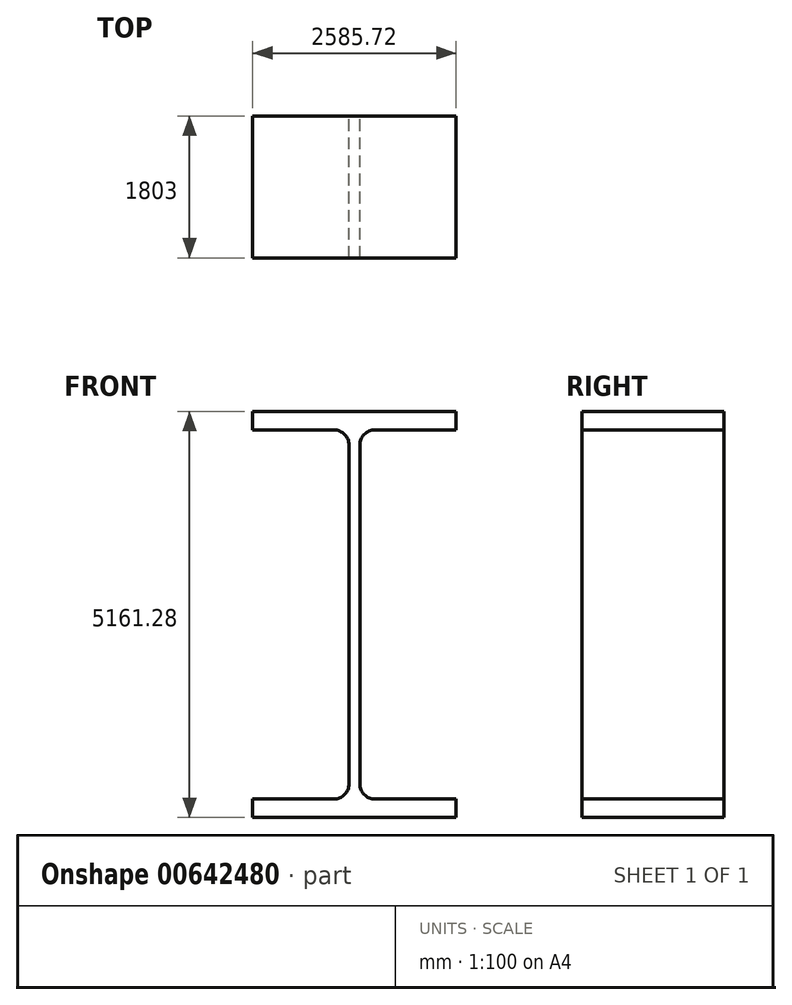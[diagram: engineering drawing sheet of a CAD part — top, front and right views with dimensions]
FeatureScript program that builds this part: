
annotation { "Feature Type Name" : "Feature", "Feature Type Description" : "" }
export const myFeature = defineFeature(function(context is Context, id is Id, definition is map)
    precondition{}
    {
        {
            var Q0;
            Q0=qCreatedBy(makeId("Front.planeOp"),FACE);
            var sketch = newSketch(context, id + "F0", { "sketchPlane" : qUnion([Q0])});
            skLineSegment(sketch, "E0", {"start": v(-1292.86, 2580.64) * mm, "end": v(-1292.86, 2344.42) * mm});
            skLineSegment(sketch, "E1", {"start": v(-1292.86, 2344.42) * mm, "end": v(-261.62, 2344.42) * mm});
            skArc(sketch, "E2", {"start": v(-261.62, 2344.42) * mm, "mid": v(-125.12, 2287.88) * mm, "end": v(-68.58, 2151.38) * mm});
            skLineSegment(sketch, "E3", {"start": v(-68.58, 2151.38) * mm, "end": v(-68.58, -2151.38) * mm});
            skArc(sketch, "E4", {"start": v(-68.58, -2151.38) * mm, "mid": v(-125.12, -2287.88) * mm, "end": v(-261.62, -2344.42) * mm});
            skLineSegment(sketch, "E5", {"start": v(-261.62, -2344.42) * mm, "end": v(-1292.86, -2344.42) * mm});
            skLineSegment(sketch, "E6", {"start": v(-1292.86, -2344.42) * mm, "end": v(-1292.86, -2580.64) * mm});
            skLineSegment(sketch, "E7", {"start": v(-1292.86, -2580.64) * mm, "end": v(1292.86, -2580.64) * mm});
            skLineSegment(sketch, "E8", {"start": v(1292.86, -2580.64) * mm, "end": v(1292.86, -2344.42) * mm});
            skLineSegment(sketch, "E9", {"start": v(1292.86, -2344.42) * mm, "end": v(261.62, -2344.42) * mm});
            skArc(sketch, "E10", {"start": v(261.62, -2344.42) * mm, "mid": v(125.12, -2287.88) * mm, "end": v(68.58, -2151.38) * mm});
            skLineSegment(sketch, "E11", {"start": v(68.58, -2151.38) * mm, "end": v(68.58, 2151.38) * mm});
            skArc(sketch, "E12", {"start": v(68.58, 2151.38) * mm, "mid": v(125.12, 2287.88) * mm, "end": v(261.62, 2344.42) * mm});
            skLineSegment(sketch, "E13", {"start": v(261.62, 2344.42) * mm, "end": v(1292.86, 2344.42) * mm});
            skLineSegment(sketch, "E14", {"start": v(1292.86, 2344.42) * mm, "end": v(1292.86, 2580.64) * mm});
            skLineSegment(sketch, "E15", {"start": v(1292.86, 2580.64) * mm, "end": v(-1292.86, 2580.64) * mm});
            skSolve(sketch);
        }
        {
            var Q0;
            Q0=makeQuery(id+"F0.imprint","IMPRINT",FACE,{"disambiguationData":[TD([[makeQuery(id+"F0.imprint","IMPRINT",EDGE,{"derivedFrom":sQuery(id+"F0.wireOp",EDGE,"E0")}),1.0]])]});
            extrude(context, id + "F1", {"entities" : qUnion([Q0]), "depth" : 1803 * mm, "offsetDistance" : 25 * mm});
        }
    });
